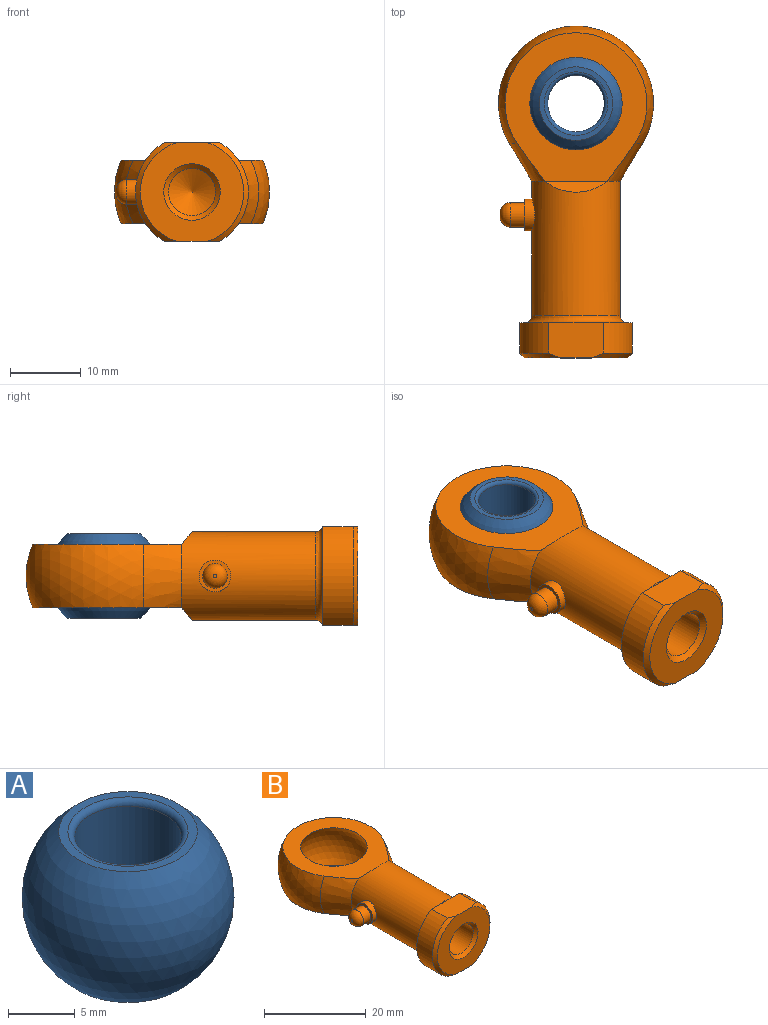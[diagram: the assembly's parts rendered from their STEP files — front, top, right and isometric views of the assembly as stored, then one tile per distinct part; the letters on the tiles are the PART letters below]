
ASSEMBLY  parts=2 mates=1
PART A: 6 faces, bbox 15.9x15.9x12 mm
  f0: plane 10.39x10.39mm, normal (0,0,1), area 21.2mm2, adj f1,f5
  f1: sphere r=7.94mm, area 598.5mm2, adj f0,f2
  f2: plane 10.39x10.39mm, normal (0,0,-1), area 21.2mm2, adj f1,f3
  f3: torus R=4.5mm, axis (0,0,1), area 20.6mm2, adj f2,f4
  f4: cylinder r=4mm len=11mm, axis (0,0,1), area 276.5mm2, adj f3,f5
  f5: torus R=4.5mm, axis (0,0,1), area 20.6mm2, adj f0,f4
PART B: 27 faces, bbox 22.1x47.1x22.1 mm
  f0: cylinder r=6.25mm len=19mm, axis (0,-1,0), area 710.5mm2, adj f1,f6,f7,f14,f17,f22
  f1: cone r=9.45mm half-angle=30.8deg, axis (0,1,0), area 60.2mm2, adj f0,f5,f15,f16
  f2: plane 14x6.11mm, normal (0,1,0), area 13.4mm2, adj f7,f9,f12,f13
  f3: cylinder r=8mm len=14mm, axis (0,-1,0), area 73.7mm2, adj f4,f8,f12,f13
  f4: cone r=8mm half-angle=45deg, axis (0,1,0), area 17.1mm2, adj f3,f11,f12,f13
  f5: sphere r=11mm, area 421mm2, adj f1,f6,f15,f16
  f6: cone r=9.45mm half-angle=30.8deg, axis (0,1,0), area 60.2mm2, adj f0,f5,f15,f16
  f7: torus R=7.25mm, axis (0,-1,0), area 64.2mm2, adj f0,f2,f8,f12,f13
  f8: plane 14x6.11mm, normal (0,1,0), area 13.4mm2, adj f3,f7,f12,f13
  f9: cylinder r=8mm len=14mm, axis (0,-1,0), area 73.7mm2, adj f2,f10,f12,f13
  f10: cone r=8mm half-angle=45deg, axis (0,1,0), area 17.1mm2, adj f9,f11,f12,f13
  f11: plane 14.65x14mm, normal (0,-1,0), area 116.4mm2, adj f4,f10,f12,f13,f21
  f12: plane 7.89x5.17mm, normal (0,0,1), area 37.7mm2, adj f2,f3,f4,f7,f8,f9,f10,f11
  f13: plane 7.89x5.17mm, normal (0,0,-1), area 37.7mm2, adj f2,f3,f4,f7,f8,f9,f10,f11
  f14: plane 8.67x1.75mm, normal (0,0.75,-0.66), area 13.9mm2, adj f0,f15
  f15: plane 21.04x20.08mm, normal (0,0,-1), area 199.3mm2, adj f1,f5,f6,f14,f18
  f16: plane 21.04x20.08mm, normal (0,0,1), area 199.3mm2, adj f1,f5,f6,f17,f18
  f17: plane 8.67x1.75mm, normal (0,0.75,0.66), area 13.9mm2, adj f0,f16
  f18: sphere r=7.94mm, area 449mm2, adj f15,f16
  f19: cone r=0mm half-angle=60deg, axis (0,-1,0), area 40.1mm2, adj f20
  f20: cylinder r=3.32mm len=19.72mm, axis (0,-1,0), area 411.9mm2, adj f19,f21
  f21: cone r=3.32mm half-angle=45deg, axis (0,-1,0), area 22mm2, adj f11,f20
  f22: cylinder r=2.25mm len=4.5mm, axis (1,0,0), area 17.1mm2, adj f0,f26
  f23: plane 0.5x0.5mm, normal (-1,0,0), area 0.2mm2, adj f24
  f24: torus R=0.25mm, axis (1,0,0), area 17.8mm2, adj f23,f25
  f25: cylinder r=1.75mm len=3.5mm, axis (1,0,0), area 22mm2, adj f24,f26
  f26: plane 4.5x4.5mm, normal (-1,0,0), area 6.3mm2, adj f22,f25
PLACE A t=(0,36,0)mm
PLACE B at identity
MATE revolute A.f4 <-> B.f5  axis (0,0,1) through (0,36,0)mm
